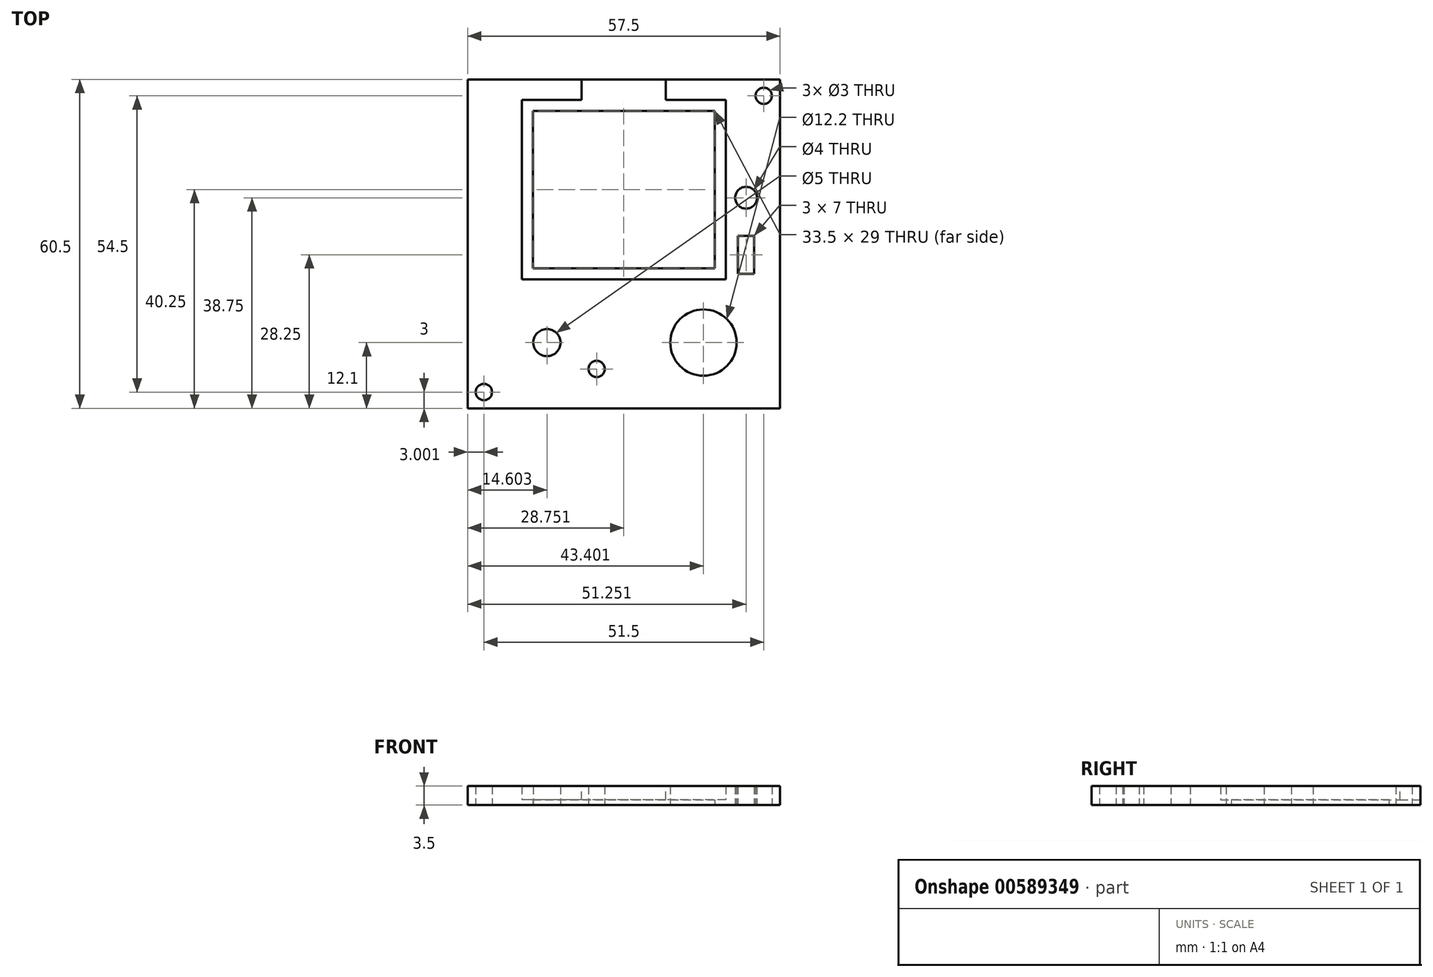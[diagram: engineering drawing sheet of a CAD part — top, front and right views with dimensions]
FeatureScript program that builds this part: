
annotation { "Feature Type Name" : "Feature", "Feature Type Description" : "" }
export const myFeature = defineFeature(function(context is Context, id is Id, definition is map)
    precondition{}
    {
        {
            var Q0;
            Q0=qCreatedBy(makeId("Top.planeOp"),FACE);
            var sketch = newSketch(context, id + "F0", { "sketchPlane" : qUnion([Q0])});
            skLineSegment(sketch, "E0.bottom", {"start": v(123.41, -30.25) * mm, "end": v(65.91, -30.25) * mm});
            skLineSegment(sketch, "E0.top", {"start": v(123.41, 30.25) * mm, "end": v(65.91, 30.25) * mm});
            skLineSegment(sketch, "E0.left", {"start": v(123.41, -30.25) * mm, "end": v(123.41, 30.25) * mm});
            skLineSegment(sketch, "E0.right", {"start": v(65.91, -30.25) * mm, "end": v(65.91, 30.25) * mm});
            skPoint(sketch, "E0.middle", {"position": v(94.66, 0) * mm});
            skLineSegment(sketch, "E1.bottom", {"start": v(113.41, -6.5) * mm, "end": v(75.91, -6.5) * mm});
            skLineSegment(sketch, "E1.top", {"start": v(113.41, 26.5) * mm, "end": v(75.91, 26.5) * mm});
            skLineSegment(sketch, "E1.left", {"start": v(113.41, -6.5) * mm, "end": v(113.41, 26.5) * mm});
            skLineSegment(sketch, "E1.right", {"start": v(75.91, -6.5) * mm, "end": v(75.91, 26.5) * mm});
            skPoint(sketch, "E1.middle", {"position": v(94.66, 10) * mm});
            skCircle(sketch, "E2", {"center": v(68.91, -27.25) * mm, "radius": 1.5 * mm});
            skCircle(sketch, "E3", {"center": v(120.41, 27.25) * mm, "radius": 1.5 * mm});
            skCircle(sketch, "E4", {"center": v(109.31, -18.15) * mm, "radius": 6.1 * mm});
            skLineSegment(sketch, "E5.bottom", {"start": v(115.66, 1.5) * mm, "end": v(118.66, 1.5) * mm});
            skLineSegment(sketch, "E5.top", {"start": v(115.66, -5.5) * mm, "end": v(118.66, -5.5) * mm});
            skLineSegment(sketch, "E5.left", {"start": v(115.66, 1.5) * mm, "end": v(115.66, -5.5) * mm});
            skLineSegment(sketch, "E5.right", {"start": v(118.66, 1.5) * mm, "end": v(118.66, -5.5) * mm});
            skCircle(sketch, "E6", {"center": v(117.16, 8.5) * mm, "radius": 2 * mm});
            skPoint(sketch, "E6.centerSnap0", {"position": v(117.16, 1.5) * mm});
            skCircle(sketch, "E7", {"center": v(80.51, -18.15) * mm, "radius": 2.5 * mm});
            skCircle(sketch, "E8", {"center": v(89.66, -23) * mm, "radius": 1.5 * mm});
            skSolve(sketch);
        }
        {
            var Q0;
            Q0=makeQuery(id+"F0.imprint","IMPRINT",FACE,{"disambiguationData":[TD([[makeQuery(id+"F0.imprint","IMPRINT",EDGE,{"derivedFrom":sQuery(id+"F0.wireOp",EDGE,"E0.bottom")}),-1.0]])]});
            extrude(context, id + "F1", {"entities" : qUnion([Q0]), "depth" : 3.5 * mm});
        }
        {
            var Q0;
            Q0=makeQuery(id+"F1.opExtrude","CAP_FACE",FACE,{"disambiguationData":[OSD([sQuery(id+"F0.wireOp",EDGE,"E0.bottom"),sQuery(id+"F0.wireOp",EDGE,"E0.top"),sQuery(id+"F0.wireOp",EDGE,"E0.left"),sQuery(id+"F0.wireOp",EDGE,"E0.right"),sQuery(id+"F0.wireOp",EDGE,"E1.bottom"),sQuery(id+"F0.wireOp",EDGE,"E1.top"),sQuery(id+"F0.wireOp",EDGE,"E1.left"),sQuery(id+"F0.wireOp",EDGE,"E1.right"),sQuery(id+"F0.wireOp",EDGE,"E2"),sQuery(id+"F0.wireOp",EDGE,"E3"),sQuery(id+"F0.wireOp",EDGE,"E4"),sQuery(id+"F0.wireOp",EDGE,"E5.bottom"),sQuery(id+"F0.wireOp",EDGE,"E5.top"),sQuery(id+"F0.wireOp",EDGE,"E5.left"),sQuery(id+"F0.wireOp",EDGE,"E5.right"),sQuery(id+"F0.wireOp",EDGE,"E6"),sQuery(id+"F0.wireOp",EDGE,"E7"),sQuery(id+"F0.wireOp",EDGE,"E8")])],"isStart":false});
            var sketch = newSketch(context, id + "F2", { "sketchPlane" : qUnion([Q0])});
            skLineSegment(sketch, "E9.bottom", {"start": v(102.41, 26.5) * mm, "end": v(86.91, 26.5) * mm});
            skLineSegment(sketch, "E9.top", {"start": v(102.41, 30.25) * mm, "end": v(86.91, 30.25) * mm});
            skLineSegment(sketch, "E9.left", {"start": v(102.41, 26.5) * mm, "end": v(102.41, 30.25) * mm});
            skLineSegment(sketch, "E9.right", {"start": v(86.91, 26.5) * mm, "end": v(86.91, 30.25) * mm});
            skPoint(sketch, "E9.middle", {"position": v(94.66, 28.38) * mm});
            skPoint(sketch, "E9.middle.positionSnap0", {"position": v(94.66, 26.5) * mm});
            skPoint(sketch, "E9.centerSnap0", {"position": v(94.66, 26.5) * mm});
            skSolve(sketch);
        }
        {
            var Q0;
            Q0=makeQuery(id+"F1.opExtrude","CAP_FACE",FACE,{"disambiguationData":[OSD([sQuery(id+"F0.wireOp",EDGE,"E0.bottom"),sQuery(id+"F0.wireOp",EDGE,"E0.top"),sQuery(id+"F0.wireOp",EDGE,"E0.left"),sQuery(id+"F0.wireOp",EDGE,"E0.right"),sQuery(id+"F0.wireOp",EDGE,"E1.bottom"),sQuery(id+"F0.wireOp",EDGE,"E1.top"),sQuery(id+"F0.wireOp",EDGE,"E1.left"),sQuery(id+"F0.wireOp",EDGE,"E1.right"),sQuery(id+"F0.wireOp",EDGE,"E2"),sQuery(id+"F0.wireOp",EDGE,"E3"),sQuery(id+"F0.wireOp",EDGE,"E4"),sQuery(id+"F0.wireOp",EDGE,"E5.bottom"),sQuery(id+"F0.wireOp",EDGE,"E5.top"),sQuery(id+"F0.wireOp",EDGE,"E5.left"),sQuery(id+"F0.wireOp",EDGE,"E5.right"),sQuery(id+"F0.wireOp",EDGE,"E6"),sQuery(id+"F0.wireOp",EDGE,"E7"),sQuery(id+"F0.wireOp",EDGE,"E8")])],"isStart":true});
            var sketch = newSketch(context, id + "F3", { "sketchPlane" : qUnion([Q0])});
            skLineSegment(sketch, "E10.bottom", {"start": v(75.91, -26.5) * mm, "end": v(113.41, -26.5) * mm});
            skLineSegment(sketch, "E10.top", {"start": v(75.91, 6.5) * mm, "end": v(113.41, 6.5) * mm});
            skLineSegment(sketch, "E10.left", {"start": v(75.91, -26.5) * mm, "end": v(75.91, 6.5) * mm});
            skLineSegment(sketch, "E10.right", {"start": v(113.41, -26.5) * mm, "end": v(113.41, 6.5) * mm});
            skLineSegment(sketch, "E11.0", {"start": v(111.41, -24.5) * mm, "end": v(111.41, 4.5) * mm});
            skLineSegment(sketch, "E11.1", {"start": v(77.91, -24.5) * mm, "end": v(111.41, -24.5) * mm});
            skLineSegment(sketch, "E11.2", {"start": v(77.91, -24.5) * mm, "end": v(77.91, 4.5) * mm});
            skLineSegment(sketch, "E11.3", {"start": v(77.91, 4.5) * mm, "end": v(111.41, 4.5) * mm});
            skSolve(sketch);
        }
        {
            var Q0;
            Q0=makeQuery(id+"F3.imprint","IMPRINT",FACE,{"disambiguationData":[TD([[makeQuery(id+"F3.imprint","IMPRINT",EDGE,{"derivedFrom":sQuery(id+"F3.wireOp",EDGE,"E10.bottom")}),-1.0]])]});
            extrude(context, id + "F4", {"entities" : qUnion([Q0]), "operationType" : NewBodyOperationType.ADD, "oppositeDirection" : true, "depth" : 1 * mm});
        }
        {
            var Q0;
            Q0=makeQuery(id+"F2.imprint","IMPRINT",FACE,{"disambiguationData":[TD([[makeQuery(id+"F2.imprint","IMPRINT",EDGE,{"derivedFrom":sQuery(id+"F2.wireOp",EDGE,"E9.bottom")}),-1.0]])]});
            extrude(context, id + "F5", {"entities" : qUnion([Q0]), "operationType" : NewBodyOperationType.REMOVE, "oppositeDirection" : true, "depth" : 2.5 * mm});
        }
    });
